# Revit family: 210_CAD O Integral EI 35 VT 15
name_source: partatom
category: Mechanical Equipment
units: mm (PartAtom-declared; Revit-internal decimal feet)

## family parameters
Always vertical = Yes
Cut with Voids When Loaded = No
Part Type = Breaks Into
Room Calculation Point = No
Round Connector Dimension = Use Diameter
Shared = No
Work Plane-Based = No

## types (1)
- CAD O Integral EI 35 VT 15
    AA1 = 950 mm  [stored 3.1168 ft]
    BB1 = 563 mm
    CAT0 = Yes
    D = 450 mm
    HH1 = 1540 mm  [stored 5.05249 ft]
    HH2 = 50 mm  [stored 0.164042 ft]
    HH3 = 1540 mm  [stored 5.05249 ft]
    Manufacturer = VIM
    QmdConnectorList = 221;D;231;D;241;D;251;D
    R = 225 mm  [stored 0.738189 ft]
    SPF = 1590 mm  [stored 5.21654 ft]
    SPG = 450 mm  [stored 1.47638 ft]
    SPH = 460 mm  [stored 1.50919 ft]
    SPI = 400 mm  [stored 1.31234 ft]
    SPN = 338 mm  [stored 1.10892 ft]
    SPO = 290 mm  [stored 0.951444 ft]
    W = 500 mm
    magiPartTypeId = 210
    magiProductCode = CAD O Integral EI 35 VT 15
    magiProductFamilyId = CAD O Integral EI 35 VT 15
    magiProductId = CAD O Integral EI 35 VT 15

note: [stored X ft] marks values corroborated as IEEE doubles in the binary element streams (Revit-internal decimal feet)

## geometry (parser evidence)
native form markers: Sweep x2
no freeform markers — native parametric forms only
